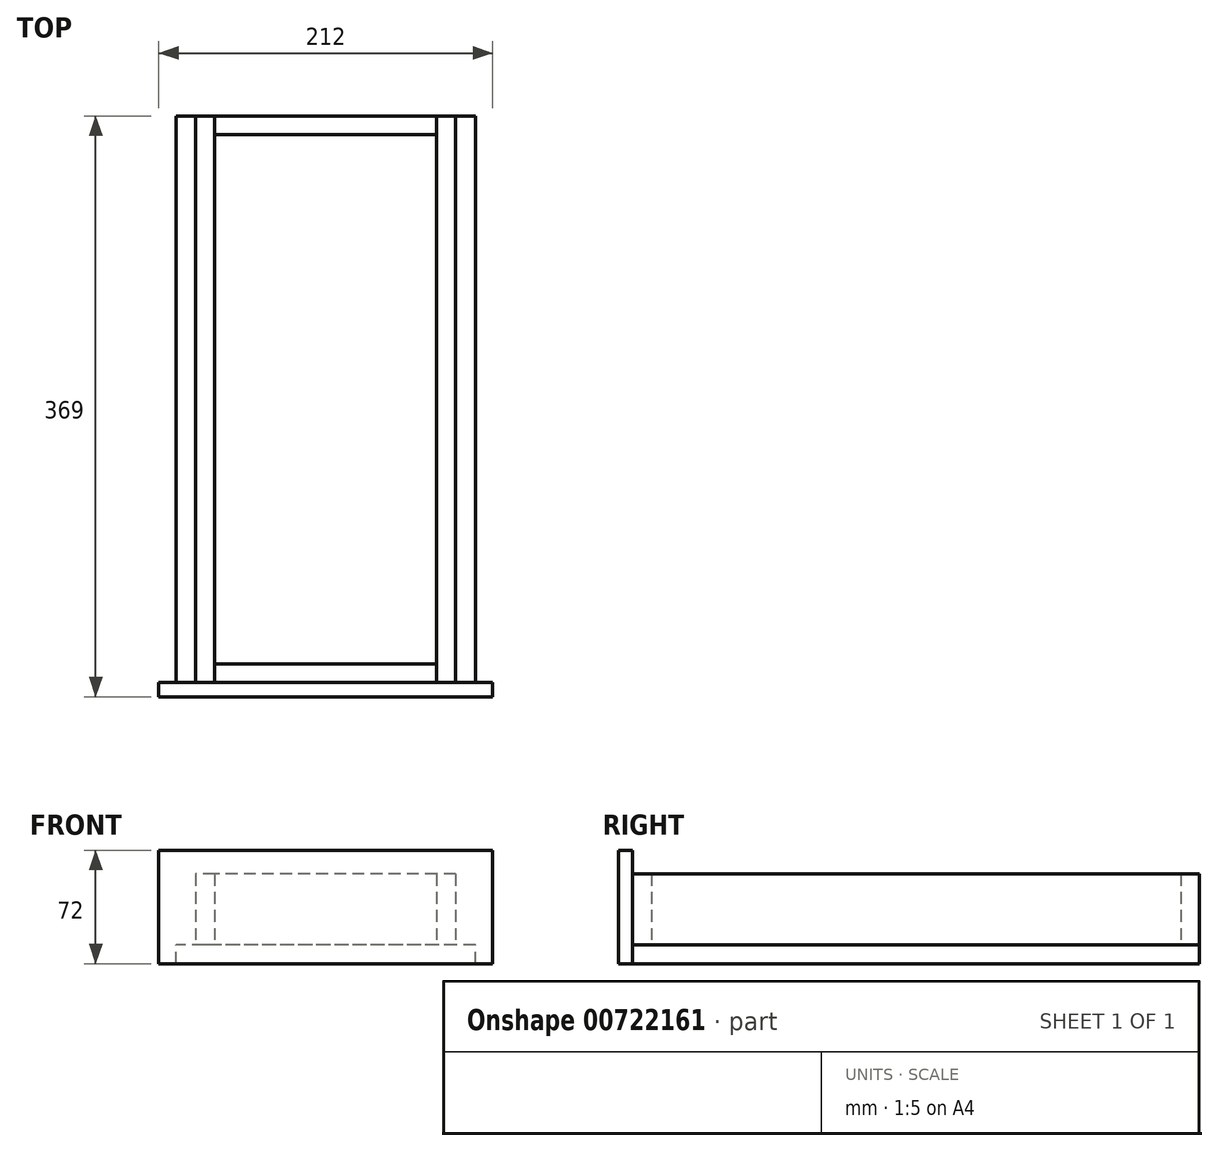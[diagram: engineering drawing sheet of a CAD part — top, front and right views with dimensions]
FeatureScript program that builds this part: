
annotation { "Feature Type Name" : "Feature", "Feature Type Description" : "" }
export const myFeature = defineFeature(function(context is Context, id is Id, definition is map)
    precondition{}
    {
        {
            var Q0;
            Q0=qCreatedBy(makeId("Top.planeOp"),FACE);
            var sketch = newSketch(context, id + "F0", { "sketchPlane" : qUnion([Q0])});
            skLineSegment(sketch, "E0.bottom", {"start": v(77.38, -180) * mm, "end": v(-87.62, -180) * mm});
            skLineSegment(sketch, "E0.top", {"start": v(77.38, 180) * mm, "end": v(-87.62, 180) * mm});
            skLineSegment(sketch, "E0.left", {"start": v(77.38, -180) * mm, "end": v(77.38, 180) * mm});
            skLineSegment(sketch, "E0.right", {"start": v(-87.62, -180) * mm, "end": v(-87.62, 180) * mm});
            skPoint(sketch, "E0.middle", {"position": v(-5.12, 0) * mm});
            skLineSegment(sketch, "E1", {"start": v(-75.62, 180) * mm, "end": v(-75.62, -180) * mm});
            skLineSegment(sketch, "E2", {"start": v(65.38, 180) * mm, "end": v(65.38, -180) * mm});
            skLineSegment(sketch, "E3", {"start": v(-75.62, -168) * mm, "end": v(65.38, -168) * mm});
            skLineSegment(sketch, "E4", {"start": v(-75.62, 168) * mm, "end": v(65.38, 168) * mm});
            skSolve(sketch);
        }
        {
            var Q0;
            {var subQ4=sQuery(id+"F0.wireOp",EDGE,"E0.left");Q0=makeQuery(id+"F0.imprint","IMPRINT",FACE,{"disambiguationData":[TD([[makeQuery(id+"F0.imprint","IMPRINT",EDGE,{"derivedFrom":subQ4}),1.0]])]});}
            var Q1;
            {var subQ4=sQuery(id+"F0.wireOp",EDGE,"E0.right");Q1=makeQuery(id+"F0.imprint","IMPRINT",FACE,{"disambiguationData":[TD([[makeQuery(id+"F0.imprint","IMPRINT",EDGE,{"derivedFrom":subQ4}),-1.0]])]});}
            extrude(context, id + "F1", {"entities" : qUnion([Q0, Q1]), "depth" : 45 * mm, "offsetDistance" : 25 * mm});
        }
        {
            var Q0;
            {var subQ5=sQuery(id+"F0.wireOp",EDGE,"E4");Q0=makeQuery(id+"F0.imprint","IMPRINT",FACE,{"disambiguationData":[TD([[makeQuery(id+"F0.imprint","IMPRINT",EDGE,{"derivedFrom":subQ5}),1.0]])]});}
            var Q1;
            {var subQ5=sQuery(id+"F0.wireOp",EDGE,"E3");Q1=makeQuery(id+"F0.imprint","IMPRINT",FACE,{"disambiguationData":[TD([[makeQuery(id+"F0.imprint","IMPRINT",EDGE,{"derivedFrom":subQ5}),-1.0]])]});}
            extrude(context, id + "F2", {"entities" : qUnion([Q0, Q1]), "depth" : 45 * mm, "offsetDistance" : 25 * mm});
        }
        {
            var Q0;
            {var subQ4=sQuery(id+"F0.wireOp",EDGE,"E0.right");Q0=makeQuery(id+"F0.imprint","IMPRINT",FACE,{"disambiguationData":[TD([[makeQuery(id+"F0.imprint","IMPRINT",EDGE,{"derivedFrom":subQ4}),-1.0]])]});}
            var sketch = newSketch(context, id + "F3", { "sketchPlane" : qUnion([Q0])});
            skLineSegment(sketch, "E5.0", {"start": v(77.38, -180) * mm, "end": v(-87.62, -180) * mm});
            skLineSegment(sketch, "E6.0", {"start": v(77.38, 180) * mm, "end": v(-87.62, 180) * mm});
            skLineSegment(sketch, "E7", {"start": v(-100.12, -180) * mm, "end": v(-100.12, 180) * mm});
            skLineSegment(sketch, "E8", {"start": v(89.88, -180) * mm, "end": v(89.88, 180) * mm});
            skLineSegment(sketch, "E9", {"start": v(89.88, 180) * mm, "end": v(77.38, 180) * mm});
            skLineSegment(sketch, "E10", {"start": v(-87.62, 180) * mm, "end": v(-100.12, 180) * mm});
            skLineSegment(sketch, "E11", {"start": v(77.38, -180) * mm, "end": v(89.88, -180) * mm});
            skLineSegment(sketch, "E12", {"start": v(-87.62, -180) * mm, "end": v(-100.12, -180) * mm});
            skSolve(sketch);
        }
        {
            var Q0;
            Q0 = qSketchRegion(id + "F3", true);
            extrude(context, id + "F4", {"entities" : qUnion([Q0]), "oppositeDirection" : true, "depth" : 12 * mm, "offsetDistance" : 25 * mm});
        }
        {
            var Q0;
            Q0=makeQuery(id+"F2.opExtrude","SWEPT_FACE",FACE,{"disambiguationData":[OSD([sQuery(id+"F0.wireOp",EDGE,"E0.bottom")])]});
            var sketch = newSketch(context, id + "F5", { "sketchPlane" : qUnion([Q0])});
            skLineSegment(sketch, "E13.0", {"start": v(89.88, -12) * mm, "end": v(-100.12, -12) * mm});
            skLineSegment(sketch, "E14", {"start": v(-100.12, -12) * mm, "end": v(-111.12, -12) * mm});
            skLineSegment(sketch, "E15", {"start": v(-111.12, -12) * mm, "end": v(-111.12, 60) * mm});
            skLineSegment(sketch, "E16", {"start": v(-111.12, 60) * mm, "end": v(100.88, 60) * mm});
            skLineSegment(sketch, "E17", {"start": v(100.88, 60) * mm, "end": v(100.88, -12) * mm});
            skLineSegment(sketch, "E18", {"start": v(100.88, -12) * mm, "end": v(89.88, -12) * mm});
            skSolve(sketch);
        }
        {
            var Q0;
            Q0 = qSketchRegion(id + "F5", true);
            extrude(context, id + "F6", {"entities" : qUnion([Q0]), "depth" : 9 * mm, "offsetDistance" : 25 * mm});
        }
    });
